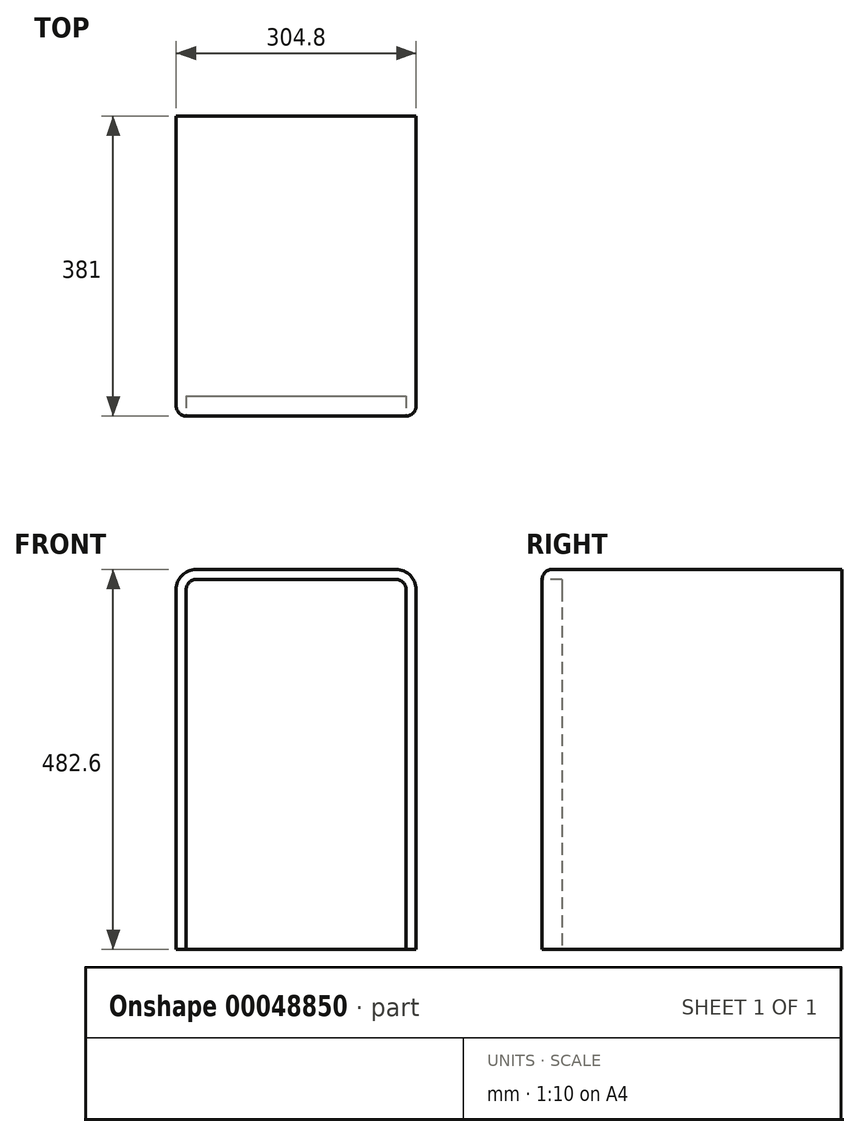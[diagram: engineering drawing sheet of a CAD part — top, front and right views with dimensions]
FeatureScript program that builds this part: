
annotation { "Feature Type Name" : "Feature", "Feature Type Description" : "" }
export const myFeature = defineFeature(function(context is Context, id is Id, definition is map)
    precondition{}
    {
        {
            var Q0;
            Q0=qCreatedBy(makeId("Top.planeOp"),FACE);
            var sketch = newSketch(context, id + "F0", { "sketchPlane" : qUnion([Q0])});
            skLineSegment(sketch, "E0.rect.bottom", {"start": v(-152.4, 190.5) * mm, "end": v(152.4, 190.5) * mm});
            skLineSegment(sketch, "E0.rect.top", {"start": v(-152.4, -190.5) * mm, "end": v(152.4, -190.5) * mm});
            skLineSegment(sketch, "E0.rect.left", {"start": v(-152.4, 190.5) * mm, "end": v(-152.4, -190.5) * mm});
            skLineSegment(sketch, "E0.rect.right", {"start": v(152.4, 190.5) * mm, "end": v(152.4, -190.5) * mm});
            skPoint(sketch, "E0.rect.middle", {"position": v(0, 0) * mm});
            skSolve(sketch);
        }
        {
            var Q0;
            Q0=makeQuery(id+"F0.imprint","IMPRINT",FACE,{"disambiguationData":[TD([[makeQuery(id+"F0.imprint","IMPRINT",EDGE,{"derivedFrom":sQuery(id+"F0.wireOp",EDGE,"E0.rect.bottom")}),-1.0]])]});
            extrude(context, id + "F1", {"entities" : qUnion([Q0]), "depth" : 482.6 * mm});
        }
        {
            var Q0;
            Q0=makeQuery(id+"F1.opExtrude","CAP_EDGE",EDGE,{"disambiguationData":[OSD([sQuery(id+"F0.wireOp",EDGE,"E0.rect.left")])],"isStart":false});
            var Q1;
            Q1=makeQuery(id+"F1.opExtrude","CAP_EDGE",EDGE,{"disambiguationData":[OSD([sQuery(id+"F0.wireOp",EDGE,"E0.rect.right")])],"isStart":false});
            fillet(context, id + "F2", {"entities" : qUnion([Q0, Q1]), "radius" : 25.4 * mm, "tangentPropagation" : true, "allowEdgeOverflow" : false});
        }
        {
            var Q0;
            Q0=makeQuery(id+"F1.opExtrude","SWEPT_EDGE",EDGE,{"disambiguationData":[OSD([sQuery(id+"F0.wireOp",EDGE,"E0.rect.top"),sQuery(id+"F0.wireOp",EDGE,"E0.rect.left")])]});
            var Q1;
            Q1=makeQuery(id+"F2.opFillet","BLEND_EDGE",EDGE,{"blendedFrom":[makeQuery(id+"F1.opExtrude","CAP_EDGE",EDGE,{"disambiguationData":[OSD([sQuery(id+"F0.wireOp",EDGE,"E0.rect.left")])],"isStart":false}),makeQuery(id+"F1.opExtrude","SWEPT_FACE",FACE,{"disambiguationData":[OSD([sQuery(id+"F0.wireOp",EDGE,"E0.rect.top")])]})],"blendedInto":[makeQuery(id+"F1.opExtrude","SWEPT_FACE",FACE,{"disambiguationData":[OSD([sQuery(id+"F0.wireOp",EDGE,"E0.rect.top")])]})]});
            var Q2;
            Q2=makeQuery(id+"F1.opExtrude","CAP_EDGE",EDGE,{"disambiguationData":[OSD([sQuery(id+"F0.wireOp",EDGE,"E0.rect.top")])],"isStart":false});
            var Q3;
            Q3=makeQuery(id+"F2.opFillet","BLEND_EDGE",EDGE,{"blendedFrom":[makeQuery(id+"F1.opExtrude","CAP_EDGE",EDGE,{"disambiguationData":[OSD([sQuery(id+"F0.wireOp",EDGE,"E0.rect.right")])],"isStart":false}),makeQuery(id+"F1.opExtrude","SWEPT_FACE",FACE,{"disambiguationData":[OSD([sQuery(id+"F0.wireOp",EDGE,"E0.rect.top")])]})],"blendedInto":[makeQuery(id+"F1.opExtrude","SWEPT_FACE",FACE,{"disambiguationData":[OSD([sQuery(id+"F0.wireOp",EDGE,"E0.rect.top")])]})]});
            var Q4;
            Q4=makeQuery(id+"F1.opExtrude","SWEPT_EDGE",EDGE,{"disambiguationData":[OSD([sQuery(id+"F0.wireOp",EDGE,"E0.rect.top"),sQuery(id+"F0.wireOp",EDGE,"E0.rect.right")])]});
            fillet(context, id + "F3", {"entities" : qUnion([Q0, Q1, Q2, Q3, Q4]), "radius" : 12.7 * mm, "tangentPropagation" : true, "allowEdgeOverflow" : false});
        }
        {
            var Q0;
            Q0=makeQuery(id+"F1.opExtrude","SWEPT_FACE",FACE,{"disambiguationData":[OSD([sQuery(id+"F0.wireOp",EDGE,"E0.rect.top")])]});
            extrude(context, id + "F4", {"entities" : qUnion([Q0]), "operationType" : NewBodyOperationType.REMOVE, "oppositeDirection" : true, "depth" : 25.4 * mm});
        }
        {
            var Q0;
            Q0=makeQuery(id+"F4.boolean.opBoolean","COPY",FACE,{"derivedFrom":makeQuery(id+"F4.opExtrude","CAP_FACE",FACE,{"disambiguationData":[OSD([sQuery(id+"F0.wireOp",EDGE,"E0.rect.top")])],"isStart":false})});
            var sketch = newSketch(context, id + "F5", { "sketchPlane" : qUnion([Q0])});
            skPoint(sketch, "E1", {"position": v(-139.7, 228.6) * mm});
            skLineSegment(sketch, "E2", {"start": v(-139.7, 228.6) * mm, "end": v(139.7, 228.6) * mm, "construction": true});
            skPoint(sketch, "E3", {"position": v(0, 469.9) * mm});
            skLineSegment(sketch, "E4", {"start": v(0, 469.9) * mm, "end": v(0, 0) * mm, "construction": true});
            skCircle(sketch, "E5", {"center": v(0, 228.6) * mm, "radius": 50.8 * mm});
            skSolve(sketch);
        }
        {
            var Q0;
            Q0=sQuery(id+"F5.wireOp",EDGE,"E5");
            extrude(context, id + "F6", {"bodyType" : ToolBodyType.SURFACE, "surfaceEntities" : qUnion([Q0]), "depth" : 25.4 * mm});
        }
    });
